# Revit family: Civil-Drainage-Channel-ACO-RoadDrain 100_Watermarked
name_source: partatom
category: Generic Models
revit_build: Autodesk Revit 2013 (Build: 20120221_2030(x64)
units: mm (PartAtom-declared; Revit-internal decimal feet)

## types (12) — shared parameters
Assembly Code = D2040
Fax = +44 (0)1462 815895
Installation guidelines = http://www.aco.co.uk
Maintenance guidelines = http://www.aco.co.uk
Model = ACO RoadDrain 100 PD100F
Model Description = Monolithic Channel drainage system
Price = POA - contact ACO
Product Page URL = http://www.aco.co.uk
Product brochure = http://www.aco.co.uk
Revision = 1
SerialNumber = 0.000000
TagNumber = 0.000000
Telephone = +44 (0)1462 816666
URL = www.aco.co.uk
zero-valued in all types: Cost, Straight Void Start

## per-type parameters (varying)
- 32101 - PD100 F 10.1 Channel 500mm LG: 32900 - Sump Unit=No; ACO Hydraulic Design Software=http://www.acodesign.co.uk; Access unit=No; Channel 160mm Wide=Yes; Channel C.S.A=0.012m²; Channel Colour=Black; Channel Material=Vienite® Synthetic Resin Concrete; Channel Recyclable=Fully recyclable; Channel Recycled Material Content=20% minimum; Closing End Cap=No; Concrete Surround Volume - Load Class F 900 - Concrete Pavement=0.22m³; Grating 500mm=No; Grating Recyclable=Fully recyclable; Grating Recycled Material Content=Between 40% - 90%; Hydraulic Performance=http://www.aco.co.uk; I/O End Cap Void=3000 mm  [stored 9.84252 ft]; Inlet Outlet end cap_350 high=No; Inlet Outlet end cap_450 high=No; Installation - Concrete Grade=Refer to brochure; Invert Depth=225mm; Invert Depth.=175 mm; Load Class=A 15 - F 900; Manufacturer=ACO Technologies plc - ACO Water Management Division; Product Code=32101; Product Dimensions=500mm x 160mm x 250mm (LxWxH); Product Standard=BE EN1433:2002, CE Marked, Kitemarked; Product Weight=22.4 Kg; Total Depth=250 mm  [stored 0.82021 ft]; Type Comments=ACO RoadDrain 100 PD100F 10.1 Constant Depth Channel 500mm Long; Void Depth=-250 mm  [stored -0.82021 ft]
- 32201 - PD100 F 20.1 Channel 500mm LG: 32900 - Sump Unit=No; ACO Hydraulic Design Software=http://www.acodesign.co.uk; Access unit=No; Channel 160mm Wide=Yes; Channel C.S.A=0.017m²; Channel Colour=Black; Channel Material=Vienite® Synthetic Resin Concrete; Channel Recyclable=Fully recyclable; Channel Recycled Material Content=20% minimum; Closing End Cap=No; Concrete Surround Volume - Load Class F 900 - Concrete Pavement=0.24m³; Grating 500mm=No; Grating Recyclable=Fully recyclable; Grating Recycled Material Content=Between 40% - 90%; Hydraulic Performance=http://www.aco.co.uk; I/O End Cap Void=3005 mm; Inlet Outlet end cap_350 high=No; Inlet Outlet end cap_450 high=No; Installation - Concrete Grade=Refer to brochure; Invert Depth=275mm; Invert Depth.=225 mm; Load Class=A 15 - F 900; Manufacturer=ACO Technologies plc - ACO Water Management Division; Product Code=32201; Product Dimensions=500mm x 160mm x 300mm (LxWxH); Product Standard=BE EN1433:2002, CE Marked, Kitemarked; Product Weight=24.5 Kg; Total Depth=300 mm; Type Comments=ACO RoadDrain 100 PD100F 20.1 Constant Depth Channel 500mm Long; Void Depth=-300 mm
- 32301 - PD100 F 30.1 Channel 500mm LG: 32900 - Sump Unit=No; ACO Hydraulic Design Software=http://www.acodesign.co.uk; Access unit=No; Channel 160mm Wide=Yes; Channel C.S.A=0.022m²; Channel Colour=Black; Channel Material=Vienite® Synthetic Resin Concrete; Channel Recyclable=Fully recyclable; Channel Recycled Material Content=20% minimum; Closing End Cap=No; Concrete Surround Volume - Load Class F 900 - Concrete Pavement=0.26m³; Grating 500mm=No; Grating Recyclable=Fully recyclable; Grating Recycled Material Content=Between 40% - 90%; Hydraulic Performance=http://www.aco.co.uk; I/O End Cap Void=3010 mm; Inlet Outlet end cap_350 high=No; Inlet Outlet end cap_450 high=No; Installation - Concrete Grade=Refer to brochure; Invert Depth=325mm; Invert Depth.=275 mm; Load Class=A 15 - F 900; Manufacturer=ACO Technologies plc - ACO Water Management Division; Product Code=32301; Product Dimensions=500mm x 160mm x 350mm (LxWxH); Product Standard=BE EN1433:2002, CE Marked, Kitemarked; Product Weight=26.6 Kg; Total Depth=350 mm; Type Comments=ACO RoadDrain 100 PD100F 30.1 Constant Depth Channel 500mm Long; Void Depth=-350 mm  [stored -1.14829 ft]
- 32401 - PD100 F 40.1 Channel 500mm LG: 32900 - Sump Unit=No; ACO Hydraulic Design Software=http://www.acodesign.co.uk; Access unit=No; Channel 160mm Wide=Yes; Channel C.S.A=0.027m²; Channel Colour=Black; Channel Material=Vienite® Synthetic Resin Concrete; Channel Recyclable=Fully recyclable; Channel Recycled Material Content=20% minimum; Closing End Cap=No; Concrete Surround Volume - Load Class F 900 - Concrete Pavement=0.28m³; Grating 500mm=No; Grating Recyclable=Fully recyclable; Grating Recycled Material Content=Between 40% - 90%; Hydraulic Performance=http://www.aco.co.uk; I/O End Cap Void=3250 mm; Inlet Outlet end cap_350 high=No; Inlet Outlet end cap_450 high=No; Installation - Concrete Grade=Refer to brochure; Invert Depth=375mm; Invert Depth.=325 mm; Load Class=A 15 - F 900; Manufacturer=ACO Technologies plc - ACO Water Management Division
ACO Technologies plc - ACO Water Management Division; Product Code=32401; Product Dimensions=500mm x 160mm x 400mm (LxWxH); Product Standard=BE EN1433:2002, CE Marked, Kitemarked; Product Weight=28.6 Kg; Total Depth=400 mm  [stored 1.31234 ft]; Type Comments=ACO RoadDrain 100 PD100F 40.1 Constant Depth Channel 500mm Long; Void Depth=-400 mm
- 32501 - PD100 F 50.1 Channel 500mm LG: 32900 - Sump Unit=No; ACO Hydraulic Design Software=http://www.acodesign.co.uk; Access unit=No; Channel 160mm Wide=Yes; Channel C.S.A=0.032m²; Channel Colour=Black; Channel Material=Vienite® Synthetic Resin Concrete; Channel Recyclable=Fully recyclable; Channel Recycled Material Content=20% minimum; Closing End Cap=No; Concrete Surround Volume - Load Class F 900 - Concrete Pavement=0.30m³; Grating 500mm=No; Grating Recyclable=Fully recyclable; Grating Recycled Material Content=Between 40% - 90%; Hydraulic Performance=http://www.aco.co.uk; I/O End Cap Void=3450 mm; Inlet Outlet end cap_350 high=No; Inlet Outlet end cap_450 high=No; Installation - Concrete Grade=Refer to brochure; Invert Depth=425mm; Invert Depth.=375 mm; Load Class=A 15 - F 900; Manufacturer=ACO Technologies plc - ACO Water Management Division; Product Code=32501; Product Dimensions=500mm x 160mm x 450mm (LxWxH); Product Standard=BE EN1433:2002, CE Marked, Kitemarked; Product Weight=30.7 Kg; Total Depth=450 mm; Type Comments=ACO RoadDrain 100 PD100F 50.1 Constant Depth Channel 500mm Long; Void Depth=-450 mm
- 32103 - PD100 F 10.3 Rodding Access 500mm LG: 32900 - Sump Unit=No; ACO Hydraulic Design Software=http://www.acodesign.co.uk; Access Cover/Frame Colour=Black; Access Cover/Frame Finish=Water Based Paint Coating; Access Cover/Frame Material=Ductile Iron; Access Cover/Frame Recyclable=Fully recyclable; Access Cover/Frame Recycled Material Content=Between 40% - 90%; Access unit=Yes; Channel 160mm Wide=No; Channel C.S.A=0.012m²; Channel Colour=Black; Channel Material=Vienite® Synthetic Resin Concrete; Channel Recyclable=Fully recyclable; Channel Recycled Material Content=20% minimum; Closing End Cap=No; Concrete Surround Volume - Load Class F 900 - Concrete Pavement=0.22m³; Grating 500mm=No; Hydraulic Performance=http://www.aco.co.uk; I/O End Cap Void=3000 mm  [stored 9.84252 ft]; Inlet Outlet end cap_350 high=No; Inlet Outlet end cap_450 high=No; Installation - Concrete Grade=Refer to brochure; Invert Depth=225mm; Invert Depth.=175 mm; Load Class=A 15 - F 900; Manufacturer=ACO Technologies plc - ACO Water Management Division; Product Code=32103; Product Dimensions=500mm x 160mm x 250mm (LxWxH); Product Standard=BE EN1433:2002, CE Marked, Kitemarked; Product Weight=26.4 Kg; Total Depth=250 mm  [stored 0.82021 ft]; Type Comments=ACO RoadDrain 100 PD100F 10.3 Constant Depth Access Channel 500mm Long; Void Depth=-250 mm  [stored -0.82021 ft]
- 32303 - PD100 F 30.3 Rodding Access 500mm LG: 32900 - Sump Unit=No; ACO Hydraulic Design Software=http://www.acodesign.co.uk; Access Cover/Frame Colour=Black; Access Cover/Frame Finish=Water Based Paint Coating; Access Cover/Frame Material=Ductile Iron; Access Cover/Frame Recyclable=Fully recyclable; Access Cover/Frame Recycled Material Content=Between 40% - 90%; Access unit=Yes; Channel 160mm Wide=No; Channel C.S.A=0.022m²; Channel Colour=Black; Channel Material=Vienite® Synthetic Resin Concrete; Channel Recyclable=Fully recyclable; Channel Recycled Material Content=20% minimum; Closing End Cap=No; Concrete Surround Volume - Load Class F 900 - Concrete Pavement=0.26m³; Grating 500mm=No; Hydraulic Performance=http://www.aco.co.uk; I/O End Cap Void=3500 mm; Inlet Outlet end cap_350 high=No; Inlet Outlet end cap_450 high=No; Installation - Concrete Grade=Refer to brochure; Invert Depth=325mm; Invert Depth.=275 mm; Load Class=A 15 - F 900; Manufacturer=ACO Technologies plc - ACO Water Management Division; Product Code=32303; Product Dimensions=500mm x 160mm x 350mm (LxWxH); Product Standard=BE EN1433:2002, CE Marked, Kitemarked; Product Weight=31.0 Kg; Total Depth=350 mm; Type Comments=ACO RoadDrain 100 PD100F 30.3 Constant Depth Access Channel 500mm Long; Void Depth=-350 mm  [stored -1.14829 ft]
- 32503 - PD100 F 50.3 Rodding Access 500mm LG: 32900 - Sump Unit=No; ACO Hydraulic Design Software=http://www.acodesign.co.uk; Access Cover/Frame Colour=Black; Access Cover/Frame Finish=Water Based Paint Coating; Access Cover/Frame Material=Ductile Iron; Access Cover/Frame Recyclable=Fully recyclable; Access Cover/Frame Recycled Material Content=Between 40% - 90%; Access unit=Yes; Channel 160mm Wide=No; Channel C.S.A=0.032m²; Channel Colour=Black; Channel Material=Vienite® Synthetic Resin Concrete; Channel Recyclable=Fully recyclable; Channel Recycled Material Content=20% minimum; Closing End Cap=No; Concrete Surround Volume - Load Class F 900 - Concrete Pavement=0.30m³; Grating 500mm=No; Hydraulic Performance=http://www.aco.co.uk; I/O End Cap Void=3260 mm; Inlet Outlet end cap_350 high=No; Inlet Outlet end cap_450 high=No; Installation - Concrete Grade=Refer to brochure; Invert Depth=425mm; Invert Depth.=375 mm; Load Class=A 15 - F 900; Manufacturer=ACO Technologies plc - ACO Water Management Division; Product Code=32503; Product Dimensions=500mm x 160mm x 450mm (LxWxH); Product Standard=BE EN1433:2002, CE Marked, Kitemarked; Product Weight=34.6 Kg; Total Depth=450 mm; Type Comments=ACO RoadDrain 100 PD100F 50.3 Constant Depth Access Channel 500mm Long; Void Depth=-450 mm
- 32506 - PD100 F 506 Closing endcap: 32900 - Sump Unit=No; Access unit=No; Channel 160mm Wide=No; Closing End Cap=Yes; End Cap Colour=Black; End Cap Material=Vienite® Synthetic Resin Concrete; End Cap Recyclable=Fully recyclable; End Cap Recycled Material Content=20% minimum; Grating 500mm=No; I/O End Cap Void=3650 mm; Inlet Outlet end cap_350 high=No; Inlet Outlet end cap_450 high=No; Invert Depth.=175 mm; Manufacturer=ACO Technologies plc - ACO Water Management Division; Product Code=32506; Product Dimensions=25mm x 160mm x 450mm (LxWxH); Product Weight=2.8 Kg; Total Depth=250 mm  [stored 0.82021 ft]; Type Comments=ACO RoadDrain PD100 F 506 Closing End Cap; Void Depth=-450 mm
- 32308 - PD100 F 308 Inlet/outlet endcap: 32900 - Sump Unit=No; Access unit=No; Channel 160mm Wide=No; Closing End Cap=No; Connection Pipe Colour=Black; Connection Pipe Material=MDPE; Connection Pipe O.D=Ø160mm; End Cap Colour=Black; End Cap Material=Vienite® Synthetic Resin Concrete; End Cap Recyclable=Fully recyclable; End Cap Recycled Material Content=20% minimum; Grating 500mm=No; I/O End Cap Void=128.041 mm; Inlet Outlet end cap_350 high=Yes; Inlet Outlet end cap_450 high=No; Invert Depth.=175 mm; Manufacturer=ACO Technologies plc - ACO Water Management Division; Product Code=32308; Product Dimensions=25mm x 160mm x 350mm (LxWxH); Product Weight=2.2 Kg; Total Depth=250 mm  [stored 0.82021 ft]; Type Comments=ACO RoadDrain PD100 F 308 Inlet/Outlet End Cap; Void Depth=-350 mm  [stored -1.14829 ft]
- 32508 - PD100 F 508 Inlet/outlet endcap: 32900 - Sump Unit=No; Access unit=No; Channel 160mm Wide=No; Closing End Cap=No; Connection Pipe Colour=Black; Connection Pipe Material=MDPE; Connection Pipe O.D=Ø160mm; End Cap Colour=Black; End Cap Material=Vienite® Synthetic Resin Concrete; End Cap Recyclable=Fully recyclable; End Cap Recycled Material Content=20% minimum; Grating 500mm=No; I/O End Cap Void=228 mm; Inlet Outlet end cap_350 high=No; Inlet Outlet end cap_450 high=Yes; Invert Depth.=175 mm; Manufacturer=ACO Technologies plc - ACO Water Management Division; Product Code=32508; Product Dimensions=25mm x 160mm x 450mm (LxWxH); Product Weight=3.0 Kg; Total Depth=250 mm  [stored 0.82021 ft]; Type Comments=ACO RoadDrain PD100 F 508 Inlet/Outlet End Cap; Void Depth=-450 mm
- 32900 - PD900 F Sump Unit - 500mm LG: 32900 - Sump Unit=Yes; ACO Hydraulic Design Software=http://www.acodesign.co.uk; Access Cover/Frame Recyclable=Fully recyclable
Fully recyclable; Access Cover/Frame Recycled Material Content=Between 40% - 90%; Access unit=No; Channel 160mm Wide=No; Channel Colour=Black; Channel Material=Vienite® Synthetic Resin Concrete; Channel Recyclable=Fully recyclable; Channel Recycled Material Content=20% minimum; Closing End Cap=No; Grating 500mm=Yes; Grating Colour=Black; Grating Finish=Water based paint coating; Grating Material=Ductile Iron; Grating Recyclable=Fully Recyclable; Grating Recycled Material Content=Between 40% - 90%; Hydraulic Performance=http://www.aco.co.uk; I/O End Cap Void=5000 mm; Inlet Outlet end cap_350 high=No; Inlet Outlet end cap_450 high=No; Installation - Concrete Grade=Refer to brochure; Invert Depth=640mm; Invert Depth.=175 mm; Load Class=A 15 - F 900; Manufacturer=ACO Technologies plc - ACO Water Management Division; Product Code=32900; Product Dimensions=500mm x 160mm x 665mm (LxWxH); Product Standard=BE EN1433:2002, CE Marked, Kitemarked; Product Weight=43.6 Kg; Total Depth=250 mm  [stored 0.82021 ft]; Type Comments=ACO RoadDrain PD900F Sump Unit 500mm Long; Void Depth=-665 mm  [stored -2.18176 ft]

note: [stored X ft] marks values corroborated as IEEE doubles in the binary element streams (Revit-internal decimal feet)

## geometry (parser evidence)
native form markers: Sweep x3
no freeform markers — native parametric forms only
